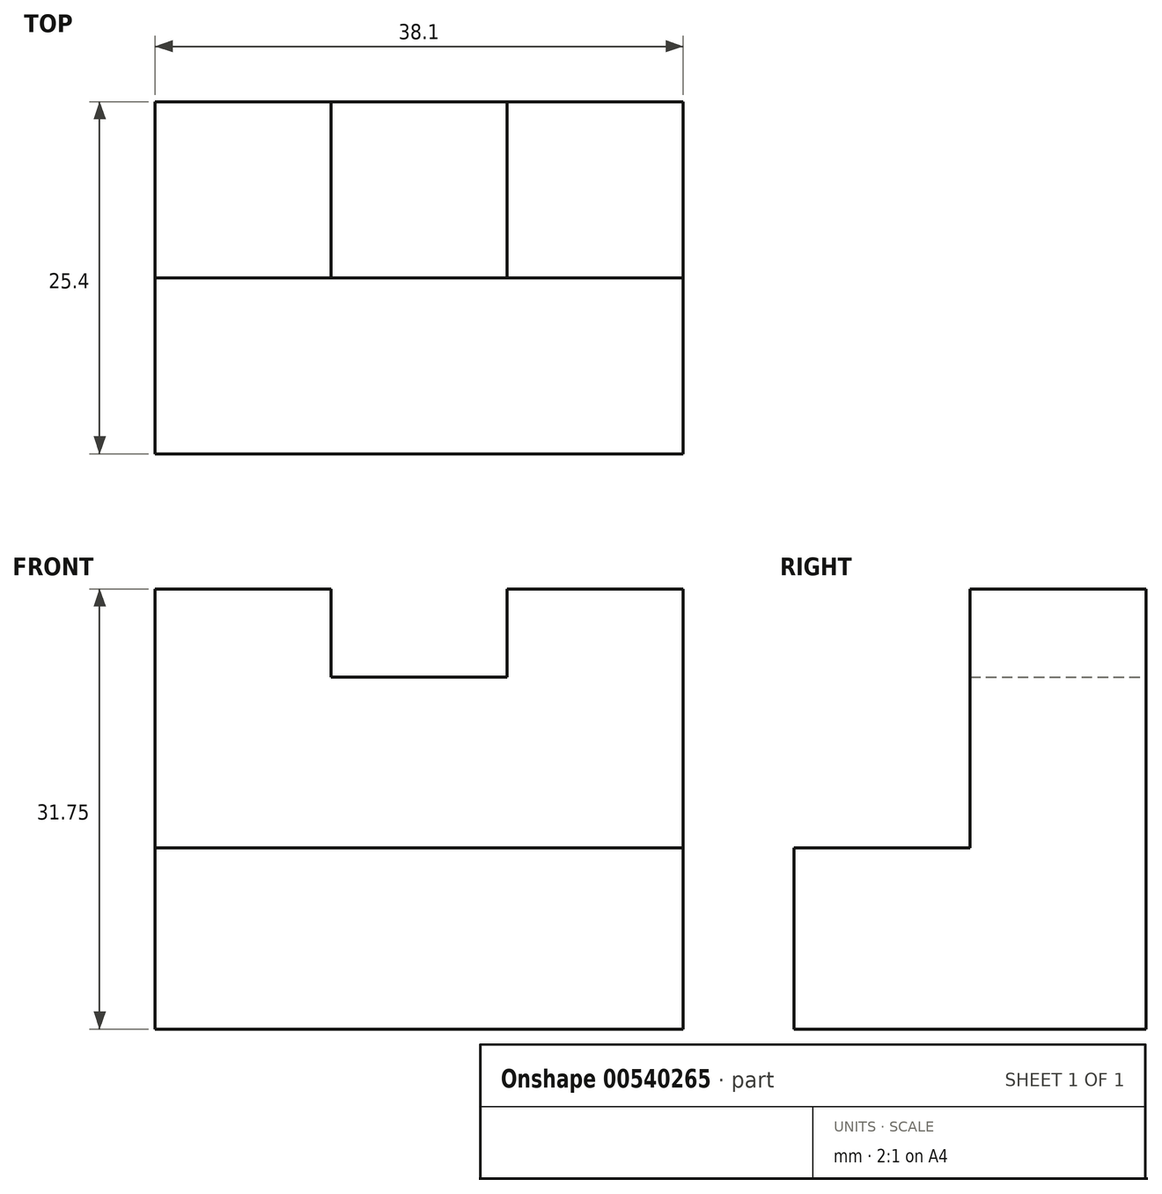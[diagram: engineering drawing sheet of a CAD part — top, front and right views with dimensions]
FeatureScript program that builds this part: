
annotation { "Feature Type Name" : "Feature", "Feature Type Description" : "" }
export const myFeature = defineFeature(function(context is Context, id is Id, definition is map)
    precondition{}
    {
        {
            var Q0;
            Q0=qCreatedBy(makeId("Front.planeOp"),FACE);
            var sketch = newSketch(context, id + "F0", { "sketchPlane" : qUnion([Q0])});
            skLineSegment(sketch, "E0", {"start": v(-59.98, 40.98) * mm, "end": v(-59.98, 9.23) * mm});
            skLineSegment(sketch, "E1", {"start": v(-59.98, 9.23) * mm, "end": v(-21.88, 9.23) * mm});
            skLineSegment(sketch, "E2", {"start": v(-21.88, 9.23) * mm, "end": v(-21.88, 40.98) * mm});
            skLineSegment(sketch, "E3", {"start": v(-21.88, 40.98) * mm, "end": v(-34.58, 40.98) * mm});
            skLineSegment(sketch, "E4", {"start": v(-34.58, 40.98) * mm, "end": v(-34.58, 34.63) * mm});
            skLineSegment(sketch, "E5", {"start": v(-34.58, 34.63) * mm, "end": v(-47.28, 34.63) * mm});
            skLineSegment(sketch, "E6", {"start": v(-47.28, 34.63) * mm, "end": v(-47.28, 40.98) * mm});
            skLineSegment(sketch, "E7", {"start": v(-47.28, 40.98) * mm, "end": v(-59.98, 40.98) * mm});
            skSolve(sketch);
        }
        {
            var Q0;
            Q0 = qSketchRegion(id + "F0", true);
            extrude(context, id + "F1", {"entities" : qUnion([Q0]), "depth" : 25.4 * mm, "offsetDistance" : 25.4 * mm});
        }
        {
            var Q0;
            Q0=qCreatedBy(makeId("Front.planeOp"),FACE);
            var sketch = newSketch(context, id + "F2", { "sketchPlane" : qUnion([Q0])});
            skLineSegment(sketch, "E8", {"start": v(-59.89, 22.26) * mm, "end": v(-21.79, 22.26) * mm});
            skSolve(sketch);
        }
        {
            var Q0;
            Q0=qCreatedBy(makeId("Front.planeOp"),FACE);
            var sketch = newSketch(context, id + "F3", { "sketchPlane" : qUnion([Q0])});
            skLineSegment(sketch, "E9", {"start": v(-60.18, 22.54) * mm, "end": v(-22.08, 22.54) * mm});
            skSolve(sketch);
        }
        {
            var Q0;
            Q0 = qSketchRegion(id + "F3", true);
            var Q1;
            Q1 = qSketchRegion(id + "F2", true);
            var Q2;
            Q2=makeQuery(id+"F1.opExtrude","CAP_FACE",FACE,{"disambiguationData":[OSD([sQuery(id+"F0.wireOp",EDGE,"E0"),sQuery(id+"F0.wireOp",EDGE,"E1"),sQuery(id+"F0.wireOp",EDGE,"E2"),sQuery(id+"F0.wireOp",EDGE,"E3"),sQuery(id+"F0.wireOp",EDGE,"E4"),sQuery(id+"F0.wireOp",EDGE,"E5"),sQuery(id+"F0.wireOp",EDGE,"E6"),sQuery(id+"F0.wireOp",EDGE,"E7")])],"isStart":false});
            extrude(context, id + "F4", {"entities" : qUnion([Q0, Q1, Q2]), "operationType" : NewBodyOperationType.REMOVE, "oppositeDirection" : true, "depth" : 12.7 * mm, "offsetDistance" : 25.4 * mm});
        }
        {
            var Q0;
            Q0=makeQuery(id+"F4.boolean.opBoolean","COPY",FACE,{"derivedFrom":makeQuery(id+"F4.opExtrude","CAP_FACE",FACE,{"disambiguationData":[OSD([sQuery(id+"F0.wireOp",EDGE,"E0"),sQuery(id+"F0.wireOp",EDGE,"E1"),sQuery(id+"F0.wireOp",EDGE,"E2"),sQuery(id+"F0.wireOp",EDGE,"E3"),sQuery(id+"F0.wireOp",EDGE,"E4"),sQuery(id+"F0.wireOp",EDGE,"E5"),sQuery(id+"F0.wireOp",EDGE,"E6"),sQuery(id+"F0.wireOp",EDGE,"E7")])],"isStart":false})});
            var sketch = newSketch(context, id + "F5", { "sketchPlane" : qUnion([Q0])});
            skLineSegment(sketch, "E10", {"start": v(-21.88, 22.29) * mm, "end": v(-59.98, 22.29) * mm});
            skSolve(sketch);
        }
        {
            var Q0;
            {var subQ0=sQuery(id+"F5.wireOp",EDGE,"E10");Q0=makeQuery(id+"F5.imprint","IMPRINT",FACE,{"disambiguationData":[TD([[makeQuery(id+"F5.imprint","IMPRINT",EDGE,{"derivedFrom":subQ0}),1.0]])]});}
            extrude(context, id + "F6", {"entities" : qUnion([Q0]), "operationType" : NewBodyOperationType.ADD, "depth" : 12.7 * mm, "offsetDistance" : 25.4 * mm});
        }
    });
